# Revit family: URA SPOT Standard - Non Permanent_Couleur
name_source: partatom
category: Luminaires
units: mm (PartAtom-declared; Revit-internal decimal feet)

## family parameters
Cote de connecteur circulaire = Utiliser le diamètre
Couper avec des vides une fois chargée = Non
Hôte = Face
Partagée = Non
Repere pour localisation dans la piece = Non
Source d'éclairage = Non
Type d'élément = Normal

## types (1)
- 100LM-1H Couleur
    Alimentation de secours = Autonome (batterie individuelle)
    Autonomie = 1H
    Batterie de rechange = 660180
    Classe de protection = II
    Conditions Générale d'Utilisation = https://export.legrand.com
    Consommation en veille = 0.0 mA
    Couleur = Noir
    Diamètre = 125 mm
    Désignation produit = BAES U22ROND ENCASTRE NON PERMANENT 100 LUMENS 1H STANDARD COULEUR
    Elévation par défaut = 2300 mm
    Fabricant = LEGRAND
    Flux lumineux utile = 100 lm
    Fonction = Éclairage d'évacuation et d'ambiance
    Fréquence = 50-60
    Hauteur = 45 mm
    Hauteur encastrement = 42 mm
    IK = 07
    IP = 42
    Matière = Plastique
    Mode de pose = Encastré
    Objet Connecté = Non
    Puissance du système = 1 W
    Référence / Modèle = LG-660032BK
    Système de contrôle = sans
    Temperature d'utilisation MIN-MAX = -5-35
    Tension = 230 AC/DC
    Type de commutation = Non permanent
    Type de connexion = Raccordement à vis
    Type de pictogramme = autre
    URL = https://www.legrand.com
    capacité des bornes = 1,5-2,5
    source lumineuse = LED non interchangeable
    état des accus = NiCd
